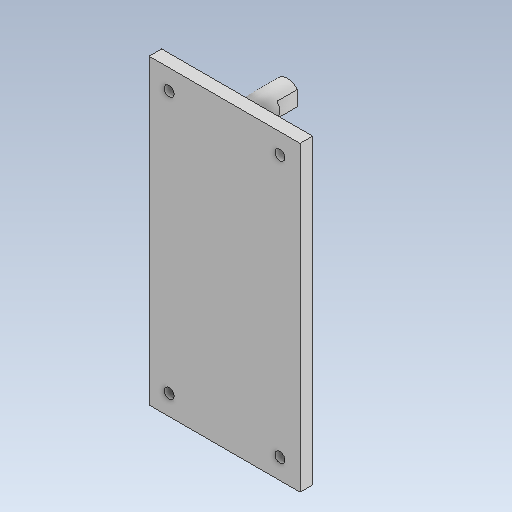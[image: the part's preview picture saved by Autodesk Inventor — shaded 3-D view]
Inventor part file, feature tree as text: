
AUTODESK INVENTOR PART (.ipt)
format: ipt  version: 2025.2 (Build 292293000, 293)  size: 295,424 bytes
history: native  units: mm
features: sketch x4, extrude x3, hole x1
ambient origin geometry x8: Origin, YZ Plane, XZ Plane, XY Plane, X Axis, Y Axis, Z Axis, Center Point
bodies: Volumenkörper1 (feature_tree)
feature tree (8):
  extrude  "Extrusion1"  Depth=60.0mm
  extrude  "Extrusion2"  Depth=10.0mm
  extrude  "Extrusion3"  Depth=50.0mm
  hole  "Bohrung1"  [1 undecoded]
  sketch  "Skizze1"  dims[d0=120.0mm d1=60.0mm]
  sketch  "Skizze2"  dims[d2=5.0mm d3=0.0mm d4=10.0mm]
  sketch  "Skizze3"  dims[d5=30.0mm d6=50.0mm]
  sketch  "Skizze4"  dims[d7=30.0mm d8=30.0mm d9=30.0mm d10=9.8mm d11=9.8mm d12=9.8mm d13=20.0mm d14=0.0mm d19=8.0mm d20=1.0mm d21=1.0mm d22=120.0mm d23=0.0mm d24=4.0mm d25=6.0mm d26=4.0mm d27=2.0mm d28=90.0deg d29=5.0mm d30=0.0mm d31=8.0mm d32=8.0mm d33=8.0mm d34=8.0mm d35=8.0mm d36=8.0mm d37=8.0mm d38=8.0mm d39=104.0mm d40=44.0mm d41=1.0mm d42=1.0mm d43=1.0mm d44=0.15mm d45=4.0mm d46=0.375mm d47=14.3117mm d48=0.75mm d49=20.594885mm d50=0.0625mm d51=0.75mm d52=0.375mm]
note: 1 required parameter value undecoded (feature->parameter linkage not recoverable at this tier; creation-order binding heuristic only, values carry confidence <= 0.55)
